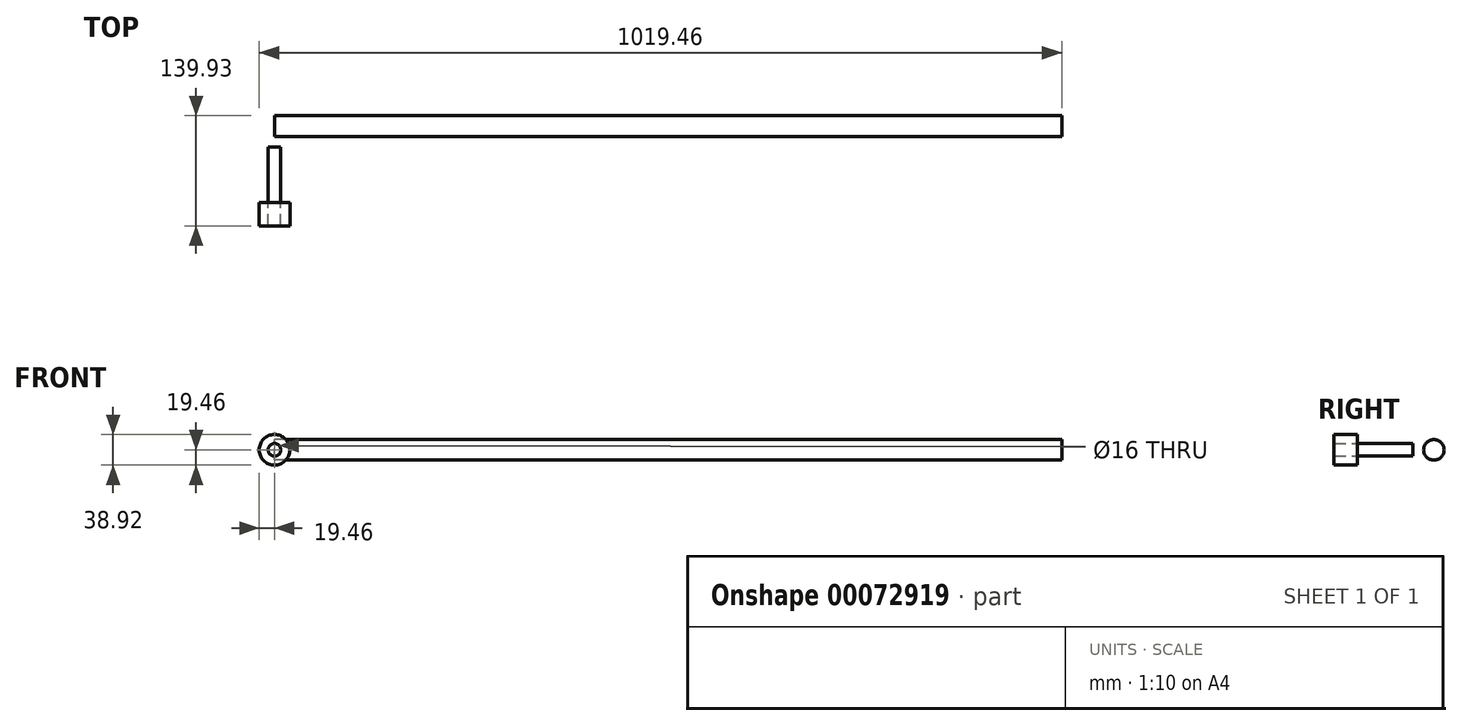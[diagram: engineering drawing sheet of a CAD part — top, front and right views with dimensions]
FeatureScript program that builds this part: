
annotation { "Feature Type Name" : "Feature", "Feature Type Description" : "" }
export const myFeature = defineFeature(function(context is Context, id is Id, definition is map)
    precondition{}
    {
        {
            var Q0;
            Q0=qCreatedBy(makeId("Top.planeOp"),FACE);
            var sketch = newSketch(context, id + "F0", { "sketchPlane" : qUnion([Q0])});
            skLineSegment(sketch, "E0", {"start": v(0, -10.32) * mm, "end": v(0, 59.68) * mm});
            skSolve(sketch);
        }
        {
            var Q0;
            Q0=qCreatedBy(makeId("Front.planeOp"),FACE);
            var sketch = newSketch(context, id + "F1", { "sketchPlane" : qUnion([Q0])});
            skCircle(sketch, "E1", {"center": v(0, 0) * mm, "radius": 8 * mm});
            skSolve(sketch);
        }
        {
            var Q0;
            Q0=makeQuery(id+"F1.imprint","IMPRINT",FACE,{"disambiguationData":[TD([[makeQuery(id+"F1.imprint","IMPRINT",EDGE,{"derivedFrom":sQuery(id+"F1.wireOp",EDGE,"E1")}),1.0]])]});
            var Q1;
            Q1=sQuery(id+"F0.wireOp",EDGE,"E0");
            sweep(context, id + "F2", {"profiles" : qUnion([Q0]), "path" : qUnion([Q1])});
        }
        {
            var Q0;
            Q0=makeQuery(id+"F2.opSweep","CAP_FACE",FACE,{"disambiguationData":[OSD([sQuery(id+"F0.wireOp",VERTEX,"E0.end"),sQuery(id+"F1.wireOp",EDGE,"E1")])],"isStart":false});
            var sketch = newSketch(context, id + "F3", { "sketchPlane" : qUnion([Q0])});
            skCircle(sketch, "E2", {"center": v(0, 0) * mm, "radius": 19.46 * mm});
            skSolve(sketch);
        }
        {
            var Q0;
            Q0=makeQuery(id+"F3.imprint","IMPRINT",FACE,{"disambiguationData":[TD([[makeQuery(id+"F3.imprint","IMPRINT",EDGE,{"derivedFrom":sQuery(id+"F3.wireOp",EDGE,"E2")}),1.0]])]});
            var Q1;
            Q1=makeQuery(id+"F3.imprint","IMPRINT",FACE,{"disambiguationData":[TD([[makeQuery(id+"F3.imprint","IMPRINT",EDGE,{"derivedFrom":makeQuery(id+"F2.opSweep","CAP_EDGE",EDGE,{"disambiguationData":[OSD([sQuery(id+"F0.wireOp",VERTEX,"E0.end"),sQuery(id+"F1.wireOp",EDGE,"E1")])],"isStart":false})}),-1.0]])]});
            extrude(context, id + "F4", {"entities" : qUnion([Q0, Q1]), "operationType" : NewBodyOperationType.ADD, "depth" : 30 * mm});
        }
        {
            var Q0;
            Q0=qCreatedBy(makeId("Right.planeOp"),FACE);
            var sketch = newSketch(context, id + "F5", { "sketchPlane" : qUnion([Q0])});
            skCircle(sketch, "E3", {"center": v(86.55, 0) * mm, "radius": 13.05 * mm});
            skSolve(sketch);
        }
        {
            var Q0;
            Q0 = qSketchRegion(id + "F5", true);
            extrude(context, id + "F6", {"entities" : qUnion([Q0]), "operationType" : NewBodyOperationType.ADD, "depth" : 1000 * mm});
        }
    });
